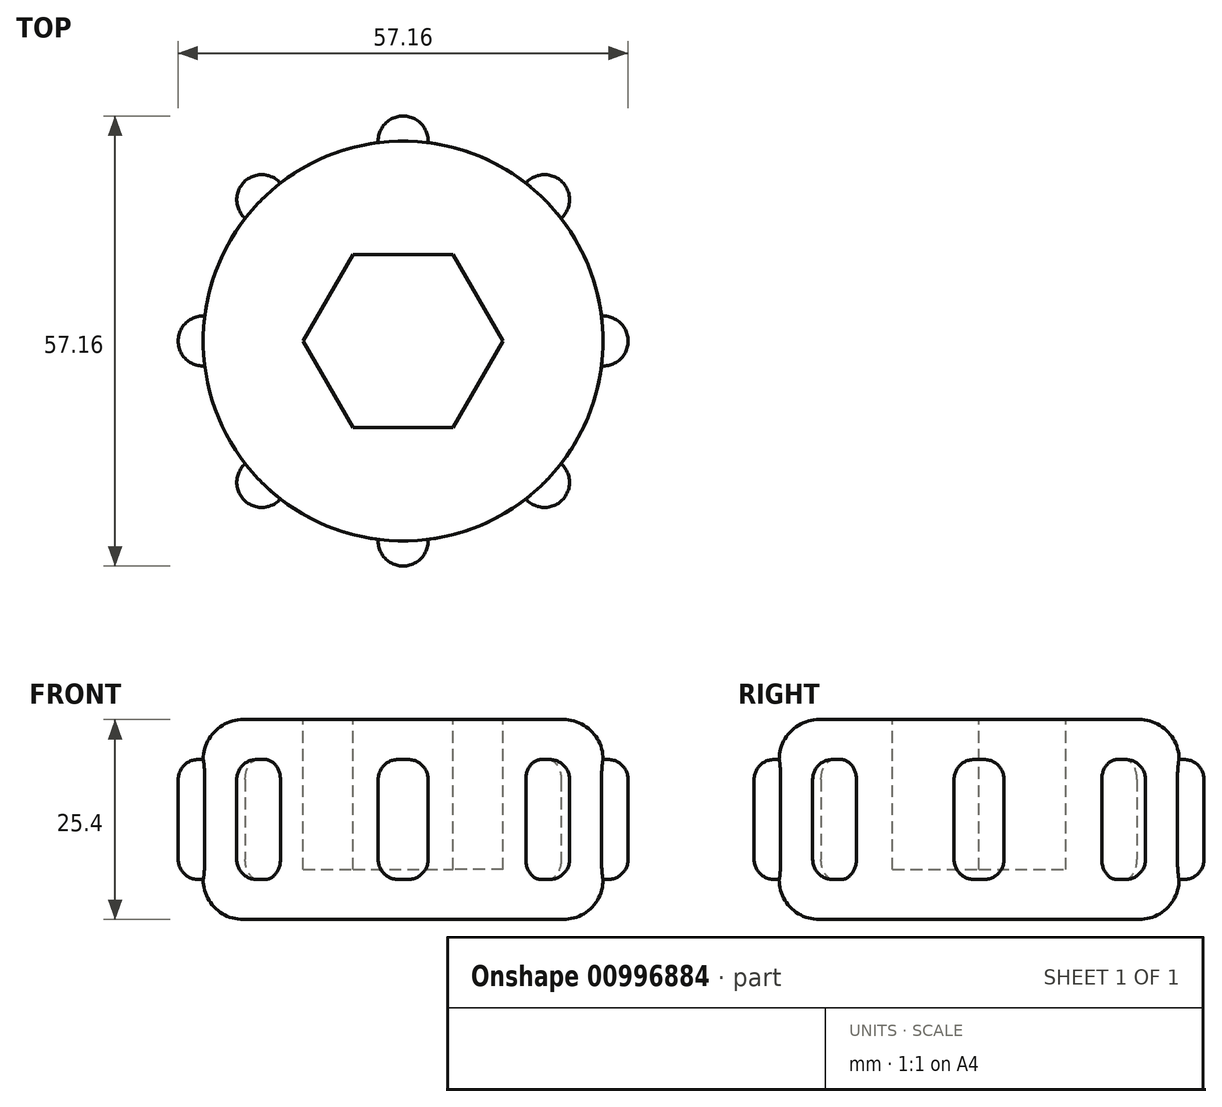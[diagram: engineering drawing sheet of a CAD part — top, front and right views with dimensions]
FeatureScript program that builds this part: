
annotation { "Feature Type Name" : "Feature", "Feature Type Description" : "" }
export const myFeature = defineFeature(function(context is Context, id is Id, definition is map)
    precondition{}
    {
        {
            var Q0;
            Q0=qCreatedBy(makeId("Top.planeOp"),FACE);
            var sketch = newSketch(context, id + "F0", { "sketchPlane" : qUnion([Q0])});
            skCircle(sketch, "E0", {"center": v(0, 0) * mm, "radius": 25.4 * mm});
            skPoint(sketch, "E1", {"position": v(0, 25.4) * mm});
            skPoint(sketch, "E2.0.midPoint", {"position": v(-6.26, 11) * mm});
            skPoint(sketch, "E3", {"position": v(0, -25.4) * mm});
            skCircle(sketch, "E4", {"center": v(0, -25.4) * mm, "radius": 3.18 * mm});
            skCircle(sketch, "E5.1.0", {"center": v(17.96, -17.96) * mm, "radius": 3.18 * mm});
            skCircle(sketch, "E5.2.0", {"center": v(25.4, 0) * mm, "radius": 3.18 * mm});
            skCircle(sketch, "E5.3.0", {"center": v(17.96, 17.96) * mm, "radius": 3.18 * mm});
            skCircle(sketch, "E5.4.0", {"center": v(0, 25.4) * mm, "radius": 3.18 * mm});
            skCircle(sketch, "E5.5.0", {"center": v(-17.96, 17.96) * mm, "radius": 3.18 * mm});
            skCircle(sketch, "E5.6.0", {"center": v(-25.4, 0) * mm, "radius": 3.18 * mm});
            skCircle(sketch, "E5.7.0", {"center": v(-17.96, -17.96) * mm, "radius": 3.18 * mm});
            skSolve(sketch);
        }
        {
            var Q0;
            Q0=makeQuery(id+"F0.imprint","IMPRINT",FACE,{"disambiguationData":[TD([[makeQuery(id+"F0.imprint","IMPRINT",EDGE,{"derivedFrom":sQuery(id+"F0.wireOp",EDGE,"E2.0")}),1.0]])]});
            var Q1;
            {var subQ0=sQuery(id+"F0.wireOp",EDGE,"E5.7.0");var subQ1=sQuery(id+"F0.wireOp",EDGE,"E0");var subQ2=makeQuery(id+"F0.imprint","INTERSECT",VERTEX,{"disambiguationData":[OD(0.0)],"derivedFrom":[subQ1,subQ0]});Q1=makeQuery(id+"F0.imprint","IMPRINT",FACE,{"disambiguationData":[TD([[makeQuery(id+"F0.imprint","IMPRINT",EDGE,{"disambiguationData":[TD([[subQ2,-1.0]])],"derivedFrom":subQ1}),1.0]])]});}
            var Q2;
            {var subQ0=sQuery(id+"F0.wireOp",EDGE,"E4");var subQ1=sQuery(id+"F0.wireOp",EDGE,"E0");var subQ2=makeQuery(id+"F0.imprint","INTERSECT",VERTEX,{"disambiguationData":[OD(0.0)],"derivedFrom":[subQ1,subQ0]});Q2=makeQuery(id+"F0.imprint","IMPRINT",FACE,{"disambiguationData":[TD([[makeQuery(id+"F0.imprint","IMPRINT",EDGE,{"disambiguationData":[TD([[subQ2,-1.0]])],"derivedFrom":subQ1}),1.0]])]});}
            var Q3;
            {var subQ0=sQuery(id+"F0.wireOp",EDGE,"E5.1.0");var subQ1=sQuery(id+"F0.wireOp",EDGE,"E0");var subQ2=makeQuery(id+"F0.imprint","INTERSECT",VERTEX,{"disambiguationData":[OD(0.0)],"derivedFrom":[subQ1,subQ0]});Q3=makeQuery(id+"F0.imprint","IMPRINT",FACE,{"disambiguationData":[TD([[makeQuery(id+"F0.imprint","IMPRINT",EDGE,{"disambiguationData":[TD([[subQ2,-1.0]])],"derivedFrom":subQ1}),1.0]])]});}
            var Q4;
            {var subQ0=sQuery(id+"F0.wireOp",EDGE,"E5.2.0");var subQ1=sQuery(id+"F0.wireOp",EDGE,"E0");var subQ2=makeQuery(id+"F0.imprint","INTERSECT",VERTEX,{"disambiguationData":[OD(0.0)],"derivedFrom":[subQ1,subQ0]});Q4=makeQuery(id+"F0.imprint","IMPRINT",FACE,{"disambiguationData":[TD([[makeQuery(id+"F0.imprint","IMPRINT",EDGE,{"disambiguationData":[TD([[subQ2,1.0]])],"derivedFrom":subQ1}),1.0]])]});}
            var Q5;
            {var subQ0=sQuery(id+"F0.wireOp",EDGE,"E5.3.0");var subQ1=sQuery(id+"F0.wireOp",EDGE,"E0");var subQ2=makeQuery(id+"F0.imprint","INTERSECT",VERTEX,{"disambiguationData":[OD(0.0)],"derivedFrom":[subQ1,subQ0]});Q5=makeQuery(id+"F0.imprint","IMPRINT",FACE,{"disambiguationData":[TD([[makeQuery(id+"F0.imprint","IMPRINT",EDGE,{"disambiguationData":[TD([[subQ2,-1.0]])],"derivedFrom":subQ1}),1.0]])]});}
            var Q6;
            {var subQ0=sQuery(id+"F0.wireOp",EDGE,"E5.4.0");var subQ1=sQuery(id+"F0.wireOp",EDGE,"E0");var subQ2=makeQuery(id+"F0.imprint","INTERSECT",VERTEX,{"disambiguationData":[OD(0.0)],"derivedFrom":[subQ1,subQ0]});Q6=makeQuery(id+"F0.imprint","IMPRINT",FACE,{"disambiguationData":[TD([[makeQuery(id+"F0.imprint","IMPRINT",EDGE,{"disambiguationData":[TD([[subQ2,-1.0]])],"derivedFrom":subQ1}),1.0]])]});}
            var Q7;
            {var subQ0=sQuery(id+"F0.wireOp",EDGE,"E5.5.0");var subQ1=sQuery(id+"F0.wireOp",EDGE,"E0");var subQ2=makeQuery(id+"F0.imprint","INTERSECT",VERTEX,{"disambiguationData":[OD(0.0)],"derivedFrom":[subQ1,subQ0]});Q7=makeQuery(id+"F0.imprint","IMPRINT",FACE,{"disambiguationData":[TD([[makeQuery(id+"F0.imprint","IMPRINT",EDGE,{"disambiguationData":[TD([[subQ2,-1.0]])],"derivedFrom":subQ1}),1.0]])]});}
            var Q8;
            {var subQ0=sQuery(id+"F0.wireOp",EDGE,"E5.6.0");var subQ1=sQuery(id+"F0.wireOp",EDGE,"E0");var subQ2=makeQuery(id+"F0.imprint","INTERSECT",VERTEX,{"disambiguationData":[OD(0.0)],"derivedFrom":[subQ1,subQ0]});Q8=makeQuery(id+"F0.imprint","IMPRINT",FACE,{"disambiguationData":[TD([[makeQuery(id+"F0.imprint","IMPRINT",EDGE,{"disambiguationData":[TD([[subQ2,-1.0]])],"derivedFrom":subQ1}),1.0]])]});}
            var Q9;
            {var subQ1=sQuery(id+"F0.wireOp",EDGE,"E0");var subQ14=sQuery(id+"F0.wireOp",EDGE,"E5.3.0");var subQ15=makeQuery(id+"F0.imprint","INTERSECT",VERTEX,{"disambiguationData":[OD(0.0)],"derivedFrom":[subQ1,subQ14]});Q9=makeQuery(id+"F0.imprint","IMPRINT",FACE,{"disambiguationData":[TD([[makeQuery(id+"F0.imprint","IMPRINT",EDGE,{"disambiguationData":[TD([[subQ15,1.0]])],"derivedFrom":subQ1}),1.0]])]});}
            extrude(context, id + "F1", {"entities" : qUnion([Q0, Q1, Q2, Q3, Q4, Q5, Q6, Q7, Q8, Q9]), "endBound" : BoundingType.SYMMETRIC, "depth" : 25.4 * mm, "offsetDistance" : 25.4 * mm});
        }
        {
            var Q0;
            {var subQ0=sQuery(id+"F0.wireOp",EDGE,"E4");var subQ1=sQuery(id+"F0.wireOp",EDGE,"E0");var subQ2=makeQuery(id+"F0.imprint","INTERSECT",VERTEX,{"disambiguationData":[OD(0.0)],"derivedFrom":[subQ1,subQ0]});Q0=makeQuery(id+"F0.imprint","IMPRINT",FACE,{"disambiguationData":[TD([[makeQuery(id+"F0.imprint","IMPRINT",EDGE,{"disambiguationData":[TD([[subQ2,-1.0]])],"derivedFrom":subQ1}),-1.0]])]});}
            var Q1;
            {var subQ0=sQuery(id+"F0.wireOp",EDGE,"E5.7.0");var subQ1=sQuery(id+"F0.wireOp",EDGE,"E0");var subQ2=makeQuery(id+"F0.imprint","INTERSECT",VERTEX,{"disambiguationData":[OD(0.0)],"derivedFrom":[subQ1,subQ0]});Q1=makeQuery(id+"F0.imprint","IMPRINT",FACE,{"disambiguationData":[TD([[makeQuery(id+"F0.imprint","IMPRINT",EDGE,{"disambiguationData":[TD([[subQ2,-1.0]])],"derivedFrom":subQ1}),-1.0]])]});}
            var Q2;
            {var subQ0=sQuery(id+"F0.wireOp",EDGE,"E5.6.0");var subQ1=sQuery(id+"F0.wireOp",EDGE,"E0");var subQ2=makeQuery(id+"F0.imprint","INTERSECT",VERTEX,{"disambiguationData":[OD(0.0)],"derivedFrom":[subQ1,subQ0]});Q2=makeQuery(id+"F0.imprint","IMPRINT",FACE,{"disambiguationData":[TD([[makeQuery(id+"F0.imprint","IMPRINT",EDGE,{"disambiguationData":[TD([[subQ2,-1.0]])],"derivedFrom":subQ1}),-1.0]])]});}
            var Q3;
            {var subQ0=sQuery(id+"F0.wireOp",EDGE,"E5.5.0");var subQ1=sQuery(id+"F0.wireOp",EDGE,"E0");var subQ2=makeQuery(id+"F0.imprint","INTERSECT",VERTEX,{"disambiguationData":[OD(0.0)],"derivedFrom":[subQ1,subQ0]});Q3=makeQuery(id+"F0.imprint","IMPRINT",FACE,{"disambiguationData":[TD([[makeQuery(id+"F0.imprint","IMPRINT",EDGE,{"disambiguationData":[TD([[subQ2,-1.0]])],"derivedFrom":subQ1}),-1.0]])]});}
            var Q4;
            {var subQ0=sQuery(id+"F0.wireOp",EDGE,"E5.4.0");var subQ1=sQuery(id+"F0.wireOp",EDGE,"E0");var subQ2=makeQuery(id+"F0.imprint","INTERSECT",VERTEX,{"disambiguationData":[OD(0.0)],"derivedFrom":[subQ1,subQ0]});Q4=makeQuery(id+"F0.imprint","IMPRINT",FACE,{"disambiguationData":[TD([[makeQuery(id+"F0.imprint","IMPRINT",EDGE,{"disambiguationData":[TD([[subQ2,-1.0]])],"derivedFrom":subQ1}),-1.0]])]});}
            var Q5;
            {var subQ0=sQuery(id+"F0.wireOp",EDGE,"E5.3.0");var subQ1=sQuery(id+"F0.wireOp",EDGE,"E0");var subQ2=makeQuery(id+"F0.imprint","INTERSECT",VERTEX,{"disambiguationData":[OD(0.0)],"derivedFrom":[subQ1,subQ0]});Q5=makeQuery(id+"F0.imprint","IMPRINT",FACE,{"disambiguationData":[TD([[makeQuery(id+"F0.imprint","IMPRINT",EDGE,{"disambiguationData":[TD([[subQ2,-1.0]])],"derivedFrom":subQ1}),-1.0]])]});}
            var Q6;
            {var subQ0=sQuery(id+"F0.wireOp",EDGE,"E5.2.0");var subQ1=sQuery(id+"F0.wireOp",EDGE,"E0");var subQ2=makeQuery(id+"F0.imprint","INTERSECT",VERTEX,{"disambiguationData":[OD(0.0)],"derivedFrom":[subQ1,subQ0]});Q6=makeQuery(id+"F0.imprint","IMPRINT",FACE,{"disambiguationData":[TD([[makeQuery(id+"F0.imprint","IMPRINT",EDGE,{"disambiguationData":[TD([[subQ2,1.0]])],"derivedFrom":subQ1}),-1.0]])]});}
            var Q7;
            {var subQ0=sQuery(id+"F0.wireOp",EDGE,"E5.1.0");var subQ1=sQuery(id+"F0.wireOp",EDGE,"E0");var subQ2=makeQuery(id+"F0.imprint","INTERSECT",VERTEX,{"disambiguationData":[OD(0.0)],"derivedFrom":[subQ1,subQ0]});Q7=makeQuery(id+"F0.imprint","IMPRINT",FACE,{"disambiguationData":[TD([[makeQuery(id+"F0.imprint","IMPRINT",EDGE,{"disambiguationData":[TD([[subQ2,-1.0]])],"derivedFrom":subQ1}),-1.0]])]});}
            extrude(context, id + "F2", {"entities" : qUnion([Q0, Q1, Q2, Q3, Q4, Q5, Q6, Q7]), "operationType" : NewBodyOperationType.ADD, "endBound" : BoundingType.SYMMETRIC, "depth" : 15.24 * mm, "offsetDistance" : 25.4 * mm});
        }
        {
            var Q0;
            Q0=makeQuery(id+"F1.opExtrude","CAP_EDGE",EDGE,{"disambiguationData":[OSD([sQuery(id+"F0.wireOp",EDGE,"E0")])],"isStart":true});
            var Q1;
            Q1=makeQuery(id+"F1.opExtrude","CAP_EDGE",EDGE,{"disambiguationData":[OSD([sQuery(id+"F0.wireOp",EDGE,"E0")])],"isStart":false});
            fillet(context, id + "F3", {"entities" : qUnion([Q0, Q1]), "radius" : 5.08 * mm, "tangentPropagation" : true, "allowEdgeOverflow" : false});
        }
        {
            var Q0;
            Q0=makeQuery(id+"F1.opExtrude","CAP_FACE",FACE,{"disambiguationData":[OSD([sQuery(id+"F0.wireOp",EDGE,"E0")])],"isStart":false});
            var sketch = newSketch(context, id + "F4", { "sketchPlane" : qUnion([Q0])});
            skCircle(sketch, "E6.cCircle", {"center": v(0, 0) * mm, "radius": 11 * mm, "construction": true});
            skLineSegment(sketch, "E6.0", {"start": v(-6.35, 11) * mm, "end": v(6.35, 11) * mm});
            skLineSegment(sketch, "E6.1", {"start": v(6.35, 11) * mm, "end": v(12.7, 0) * mm});
            skLineSegment(sketch, "E6.2", {"start": v(12.7, 0) * mm, "end": v(6.35, -11) * mm});
            skLineSegment(sketch, "E6.3", {"start": v(6.35, -11) * mm, "end": v(-6.35, -11) * mm});
            skLineSegment(sketch, "E6.4", {"start": v(-6.35, -11) * mm, "end": v(-12.7, 0) * mm});
            skLineSegment(sketch, "E6.5", {"start": v(-12.7, 0) * mm, "end": v(-6.35, 11) * mm});
            skPoint(sketch, "E6.0.midPoint", {"position": v(0, 11) * mm});
            skSolve(sketch);
        }
        {
            var Q0;
            Q0=makeQuery(id+"F4.imprint","IMPRINT",FACE,{"disambiguationData":[TD([[makeQuery(id+"F4.imprint","IMPRINT",EDGE,{"derivedFrom":sQuery(id+"F4.wireOp",EDGE,"E6.0")}),-1.0]])]});
            extrude(context, id + "F5", {"entities" : qUnion([Q0]), "operationType" : NewBodyOperationType.REMOVE, "oppositeDirection" : true, "depth" : 19.05 * mm, "offsetDistance" : 25.4 * mm});
        }
        {
            var Q0;
            Q0=makeQuery(id+"F2.opExtrude","CAP_EDGE",EDGE,{"disambiguationData":[OSD([sQuery(id+"F0.wireOp",EDGE,"E5.4.0")])],"isStart":false});
            var Q1;
            Q1=makeQuery(id+"F2.opExtrude","CAP_EDGE",EDGE,{"disambiguationData":[OSD([sQuery(id+"F0.wireOp",EDGE,"E5.4.0")])],"isStart":true});
            var Q2;
            Q2=makeQuery(id+"F2.opExtrude","CAP_EDGE",EDGE,{"disambiguationData":[OSD([sQuery(id+"F0.wireOp",EDGE,"E5.3.0")])],"isStart":false});
            var Q3;
            Q3=makeQuery(id+"F2.opExtrude","CAP_EDGE",EDGE,{"disambiguationData":[OSD([sQuery(id+"F0.wireOp",EDGE,"E5.3.0")])],"isStart":true});
            var Q4;
            Q4=makeQuery(id+"F2.opExtrude","CAP_EDGE",EDGE,{"disambiguationData":[OSD([sQuery(id+"F0.wireOp",EDGE,"E5.5.0")])],"isStart":false});
            var Q5;
            Q5=makeQuery(id+"F2.opExtrude","CAP_EDGE",EDGE,{"disambiguationData":[OSD([sQuery(id+"F0.wireOp",EDGE,"E5.5.0")])],"isStart":true});
            var Q6;
            Q6=makeQuery(id+"F2.opExtrude","CAP_EDGE",EDGE,{"disambiguationData":[OSD([sQuery(id+"F0.wireOp",EDGE,"E5.2.0")])],"isStart":false});
            var Q7;
            Q7=makeQuery(id+"F2.opExtrude","CAP_EDGE",EDGE,{"disambiguationData":[OSD([sQuery(id+"F0.wireOp",EDGE,"E5.2.0")])],"isStart":true});
            var Q8;
            Q8=makeQuery(id+"F2.opExtrude","CAP_EDGE",EDGE,{"disambiguationData":[OSD([sQuery(id+"F0.wireOp",EDGE,"E5.1.0")])],"isStart":false});
            var Q9;
            Q9=makeQuery(id+"F2.opExtrude","CAP_EDGE",EDGE,{"disambiguationData":[OSD([sQuery(id+"F0.wireOp",EDGE,"E5.1.0")])],"isStart":true});
            var Q10;
            Q10=makeQuery(id+"F2.opExtrude","CAP_EDGE",EDGE,{"disambiguationData":[OSD([sQuery(id+"F0.wireOp",EDGE,"E4")])],"isStart":false});
            var Q11;
            Q11=makeQuery(id+"F2.opExtrude","CAP_EDGE",EDGE,{"disambiguationData":[OSD([sQuery(id+"F0.wireOp",EDGE,"E4")])],"isStart":true});
            var Q12;
            Q12=makeQuery(id+"F2.opExtrude","CAP_EDGE",EDGE,{"disambiguationData":[OSD([sQuery(id+"F0.wireOp",EDGE,"E5.7.0")])],"isStart":false});
            var Q13;
            Q13=makeQuery(id+"F2.opExtrude","CAP_EDGE",EDGE,{"disambiguationData":[OSD([sQuery(id+"F0.wireOp",EDGE,"E5.7.0")])],"isStart":true});
            var Q14;
            Q14=makeQuery(id+"F2.opExtrude","CAP_EDGE",EDGE,{"disambiguationData":[OSD([sQuery(id+"F0.wireOp",EDGE,"E5.6.0")])],"isStart":false});
            var Q15;
            Q15=makeQuery(id+"F2.opExtrude","CAP_EDGE",EDGE,{"disambiguationData":[OSD([sQuery(id+"F0.wireOp",EDGE,"E5.6.0")])],"isStart":true});
            fillet(context, id + "F6", {"entities" : qUnion([Q0, Q1, Q2, Q3, Q4, Q5, Q6, Q7, Q8, Q9, Q10, Q11, Q12, Q13, Q14, Q15]), "radius" : 2.54 * mm, "tangentPropagation" : true, "allowEdgeOverflow" : false});
        }
    });
